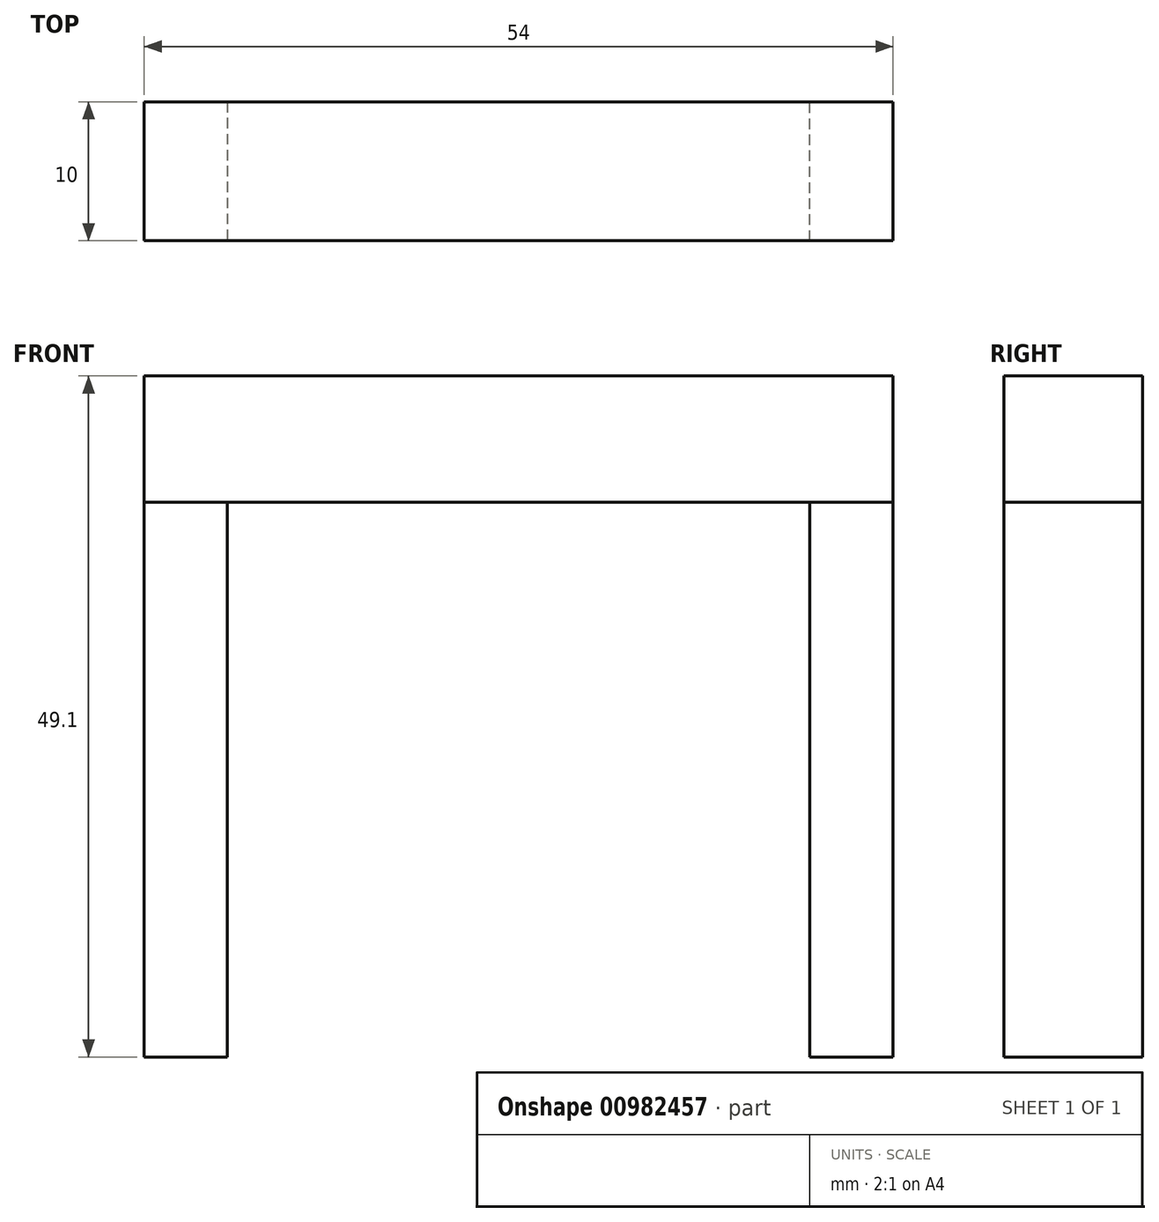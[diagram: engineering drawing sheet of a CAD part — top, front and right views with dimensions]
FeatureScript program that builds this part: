
annotation { "Feature Type Name" : "Feature", "Feature Type Description" : "" }
export const myFeature = defineFeature(function(context is Context, id is Id, definition is map)
    precondition{}
    {
        {
            var Q0;
            Q0=qCreatedBy(makeId("Top.planeOp"),FACE);
            var sketch = newSketch(context, id + "F0", { "sketchPlane" : qUnion([Q0])});
            skLineSegment(sketch, "E0", {"start": v(-50.22, 36.29) * mm, "end": v(-50.22, 26.29) * mm});
            skLineSegment(sketch, "E1", {"start": v(-50.22, 26.29) * mm, "end": v(-8.22, 26.29) * mm});
            skLineSegment(sketch, "E2", {"start": v(-8.22, 26.29) * mm, "end": v(-8.22, 36.29) * mm});
            skLineSegment(sketch, "E3", {"start": v(-8.22, 36.29) * mm, "end": v(-50.22, 36.29) * mm});
            skLineSegment(sketch, "E4", {"start": v(-13.24, 26.29) * mm, "end": v(-13.24, 8.29) * mm});
            skLineSegment(sketch, "E5", {"start": v(-13.24, 8.29) * mm, "end": v(-19.99, 8.29) * mm});
            skLineSegment(sketch, "E6", {"start": v(-19.99, 8.29) * mm, "end": v(-19.99, 26.29) * mm});
            skLineSegment(sketch, "E7", {"start": v(-19.99, 26.29) * mm, "end": v(-13.24, 26.29) * mm});
            skLineSegment(sketch, "E8", {"start": v(-13.24, 8.29) * mm, "end": v(-13.24, -5.71) * mm});
            skLineSegment(sketch, "E9", {"start": v(-13.24, -5.71) * mm, "end": v(-13.24, -19.71) * mm});
            skLineSegment(sketch, "E10", {"start": v(-13.24, -19.71) * mm, "end": v(-19.99, -19.71) * mm});
            skLineSegment(sketch, "E11", {"start": v(-19.99, -19.71) * mm, "end": v(-19.99, 8.29) * mm});
            skLineSegment(sketch, "E12", {"start": v(-13.24, -5.71) * mm, "end": v(-19.99, -5.71) * mm});
            skLineSegment(sketch, "E13", {"start": v(-13.24, -19.71) * mm, "end": v(-13.24, -25.71) * mm});
            skLineSegment(sketch, "E14", {"start": v(-13.24, -5.71) * mm, "end": v(-13.24, 0.29) * mm});
            skLineSegment(sketch, "E15", {"start": v(-13.24, 0.29) * mm, "end": v(-19.99, 0.29) * mm});
            skLineSegment(sketch, "E16", {"start": v(-19.99, 0.29) * mm, "end": v(-19.99, -25.71) * mm});
            skLineSegment(sketch, "E17", {"start": v(-19.99, -25.71) * mm, "end": v(-13.24, -25.71) * mm});
            skCircle(sketch, "E18", {"center": v(-16.26, -2.71) * mm, "radius": 3.02 * mm});
            skPoint(sketch, "E18.first.point", {"position": v(-16.61, 0.29) * mm});
            skPoint(sketch, "E18.second.point", {"position": v(-13.24, -2.71) * mm});
            skPoint(sketch, "E18.third.point", {"position": v(-16.61, -5.71) * mm});
            skCircle(sketch, "E19", {"center": v(-16.26, -22.71) * mm, "radius": 3.02 * mm});
            skPoint(sketch, "E19.first.point", {"position": v(-16.61, -19.71) * mm});
            skPoint(sketch, "E19.second.point", {"position": v(-13.24, -22.71) * mm});
            skPoint(sketch, "E19.third.point", {"position": v(-16.61, -25.71) * mm});
            skLineSegment(sketch, "E20", {"start": v(-50.22, 36.29) * mm, "end": v(-56.22, 36.29) * mm});
            skLineSegment(sketch, "E21", {"start": v(-56.22, 36.29) * mm, "end": v(-56.22, 26.29) * mm});
            skLineSegment(sketch, "E22", {"start": v(-56.22, 26.29) * mm, "end": v(-50.22, 26.29) * mm});
            skLineSegment(sketch, "E23", {"start": v(-8.22, 36.29) * mm, "end": v(-2.22, 36.29) * mm});
            skLineSegment(sketch, "E24", {"start": v(-2.22, 36.29) * mm, "end": v(-2.22, 26.29) * mm});
            skLineSegment(sketch, "E25", {"start": v(-2.22, 26.29) * mm, "end": v(-8.22, 26.29) * mm});
            skSolve(sketch);
        }
        {
            var Q0;
            Q0=makeQuery(id+"F0.imprint","IMPRINT",FACE,{"disambiguationData":[TD([[makeQuery(id+"F0.imprint","IMPRINT",EDGE,{"derivedFrom":sQuery(id+"F0.wireOp",EDGE,"E2")}),-1.0]])]});
            var Q1;
            Q1=makeQuery(id+"F0.imprint","IMPRINT",FACE,{"disambiguationData":[TD([[makeQuery(id+"F0.imprint","IMPRINT",EDGE,{"derivedFrom":sQuery(id+"F0.wireOp",EDGE,"E0")}),-1.0]])]});
            extrude(context, id + "F1", {"entities" : qUnion([Q0, Q1]), "oppositeDirection" : true, "depth" : 40 * mm, "offsetDistance" : 25 * mm});
        }
        {
            var Q0;
            Q0=makeQuery(id+"F0.imprint","IMPRINT",FACE,{"disambiguationData":[TD([[makeQuery(id+"F0.imprint","IMPRINT",EDGE,{"derivedFrom":sQuery(id+"F0.wireOp",EDGE,"E0")}),-1.0]])]});
            var Q1;
            {var subQ3=sQuery(id+"F0.wireOp",EDGE,"E0");Q1=makeQuery(id+"F0.imprint","IMPRINT",FACE,{"disambiguationData":[TD([[makeQuery(id+"F0.imprint","IMPRINT",EDGE,{"derivedFrom":subQ3}),1.0]])]});}
            var Q2;
            Q2=makeQuery(id+"F0.imprint","IMPRINT",FACE,{"disambiguationData":[TD([[makeQuery(id+"F0.imprint","IMPRINT",EDGE,{"derivedFrom":sQuery(id+"F0.wireOp",EDGE,"E2")}),-1.0]])]});
            extrude(context, id + "F2", {"entities" : qUnion([Q0, Q1, Q2]), "depth" : 9.1 * mm, "offsetDistance" : 25 * mm});
        }
    });
